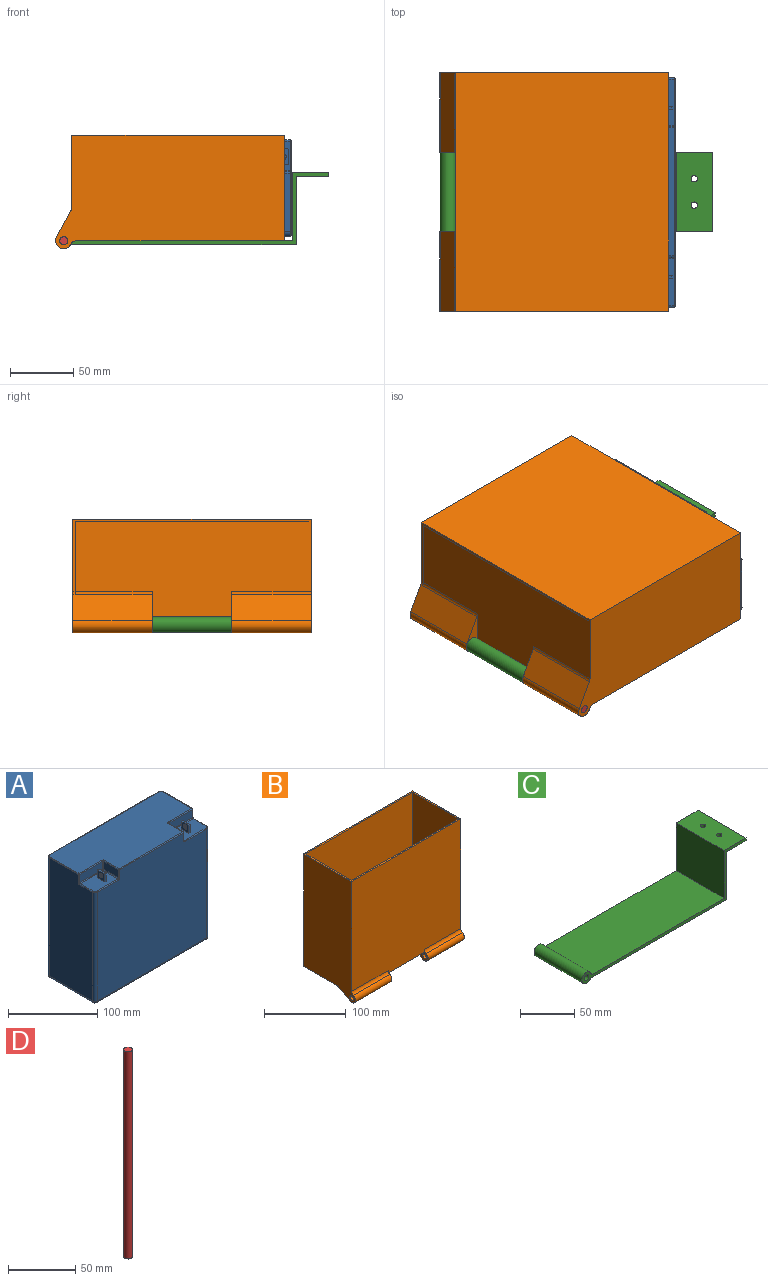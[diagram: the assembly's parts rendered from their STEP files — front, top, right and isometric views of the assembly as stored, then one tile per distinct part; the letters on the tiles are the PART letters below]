
ASSEMBLY  parts=4 mates=3
PART A: 78 faces, bbox 181.6x76.6x167 mm
  f0: plane 179x74mm, normal (0,0,1), area 11284.4mm2, adj f49,f50,f54,f59,f64,f68,f69,f71
  f1: plane 173.8x162.4mm, normal (0,-1,0), area 27282.9mm2, adj f28,f30,f31,f40,f44,f48,f52,f56
  f2: plane 173.8x162.4mm, normal (0,1,0), area 28225.1mm2, adj f33,f37,f39,f72
  f3: plane 162.4x68.8mm, normal (-1,0,0), area 10880.1mm2, adj f30,f36,f39,f47,f51,f55,f64
  f4: plane 162.4x68.8mm, normal (1,0,0), area 10880.2mm2, adj f28,f32,f33,f65,f70,f73,f77
  f5: plane 173.8x68.8mm, normal (0,0,-1), area 11957.4mm2, adj f31,f32,f36,f37
  f6: plane 37.4x23.2mm, normal (0,0,1), area 842.2mm2, adj f12,f13,f14,f15,f56,f57,f61,f65
  f7: plane 37.4x11mm, normal (0,-1,0), area 411.4mm2, adj f66,f67,f73,f74
  f8: plane 23.2x11mm, normal (1,0,0), area 255.2mm2, adj f57,f58,f67,f68
  f9: plane 36.4x23.2mm, normal (0,0,1), area 818.9mm2, adj f20,f21,f22,f23,f40,f41,f43,f46
  f10: plane 36.4x11.01mm, normal (0,-1,0), area 400.6mm2, adj f45,f46,f54,f55
  f11: plane 23.2x11.01mm, normal (-1,0,0), area 255.3mm2, adj f41,f45,f48,f49
  f12: plane 12x11mm, normal (-1,0,0), area 107.8mm2, adj f6,f13,f15,f16,f17,f18,f19
  f13: plane 10x2mm, normal (0,-1,0), area 20mm2, adj f6,f12,f14,f17
  f14: plane 12x11mm, normal (1,0,0), area 107.8mm2, adj f6,f13,f15,f16,f17,f18,f19
  f15: plane 10x2mm, normal (0,1,0), area 20mm2, adj f6,f12,f14,f18
  f16: plane 10x2mm, normal (0,0,1), area 20mm2, adj f12,f14,f17,f18
  f17: cylinder r=1mm len=2mm, axis (-1,0,0), area 3.1mm2, adj f12,f13,f14,f16
  f18: cylinder r=1mm len=2mm, axis (1,0,0), area 3.1mm2, adj f12,f14,f15,f16
  f19: cylinder r=2.75mm len=5.5mm, axis (1,0,0), area 34.6mm2, adj f12,f14
  f20: plane 11.99x11mm, normal (-1,0,0), area 107.7mm2, adj f9,f21,f23,f24,f25,f26,f27
  f21: plane 10x2mm, normal (0,-1,0), area 20mm2, adj f9,f20,f22,f25
  f22: plane 11.99x11mm, normal (1,0,0), area 107.7mm2, adj f9,f21,f23,f24,f25,f26,f27
  f23: plane 10x2mm, normal (0,1,0), area 20mm2, adj f9,f20,f22,f26
  f24: plane 9.99x2mm, normal (0,0,1), area 20mm2, adj f20,f22,f25,f26
  f25: cylinder r=1mm len=2mm, axis (-1,0,0), area 3.1mm2, adj f20,f21,f22,f24
  f26: cylinder r=1mm len=2mm, axis (1,0,0), area 3.1mm2, adj f20,f22,f23,f24
  f27: cylinder r=2.75mm len=5.5mm, axis (-1,0,0), area 34.6mm2, adj f20,f22
  f28: cylinder r=3.6mm len=149.4mm, axis (0,0,1), area 844.8mm2, adj f1,f4,f29,f61
  f29: sphere r=3.6mm, area 20.4mm2, adj f28,f31,f32
  f30: cylinder r=3.6mm len=149.4mm, axis (0,0,-1), area 844.8mm2, adj f1,f3,f34,f43
  f31: cylinder r=3.6mm len=173.8mm, axis (1,0,0), area 982.8mm2, adj f1,f5,f29,f34
  f32: cylinder r=3.6mm len=68.8mm, axis (0,1,0), area 389.1mm2, adj f4,f5,f29,f35
  f33: cylinder r=3.6mm len=162.4mm, axis (0,0,-1), area 918.4mm2, adj f2,f4,f35,f75
  f34: sphere r=3.6mm, area 20.4mm2, adj f30,f31,f36
  f35: sphere r=3.6mm, area 20.4mm2, adj f32,f33,f37
  f36: cylinder r=3.6mm len=68.8mm, axis (0,-1,0), area 389.1mm2, adj f3,f5,f34,f38
  f37: cylinder r=3.6mm len=173.8mm, axis (-1,0,0), area 982.8mm2, adj f2,f5,f35,f38
  f38: sphere r=3.6mm, area 20.4mm2, adj f36,f37,f39
  f39: cylinder r=3.6mm len=162.4mm, axis (0,0,1), area 918.4mm2, adj f2,f3,f38,f69
  f40: cylinder r=1mm len=33.8mm, axis (1,0,0), area 53.1mm2, adj f1,f9,f43,f44
  f41: cylinder r=1mm len=23.2mm, axis (0,-1,0), area 36.4mm2, adj f9,f11,f42,f44
  f42: sphere r=1mm, area 1.6mm2, adj f41,f45,f46
  f43: torus R=2.6mm, axis (0,0,1), area 8mm2, adj f9,f30,f40,f47
  f44: torus R=2mm, axis (0,1,0), area 3.4mm2, adj f1,f40,f41,f48
  f45: cylinder r=1mm len=11.01mm, axis (0,0,-1), area 17.3mm2, adj f10,f11,f42,f50
  f46: cylinder r=1mm len=36.4mm, axis (-1,0,0), area 57.2mm2, adj f9,f10,f42,f51
  f47: cylinder r=1mm len=20.6mm, axis (0,-1,0), area 32.4mm2, adj f3,f9,f43,f51
  f48: cylinder r=1mm len=11.01mm, axis (0,0,1), area 17.3mm2, adj f1,f11,f44,f53
  f49: cylinder r=1mm len=23.2mm, axis (0,-1,0), area 36.4mm2, adj f0,f11,f50,f53
  f50: torus R=2mm, axis (0,0,1), area 3.4mm2, adj f0,f45,f49,f54
  f51: torus R=2mm, axis (1,0,0), area 3.4mm2, adj f3,f46,f47,f55
  f52: torus R=2mm, axis (0,1,0), area 3.4mm2, adj f1,f56,f57,f58
  f53: sphere r=1mm, area 1.6mm2, adj f48,f49,f59
  f54: cylinder r=1mm len=36.4mm, axis (1,0,0), area 57.2mm2, adj f0,f10,f50,f60
  f55: cylinder r=1mm len=11.01mm, axis (0,0,-1), area 17.3mm2, adj f3,f10,f51,f60
  f56: cylinder r=1mm len=34.8mm, axis (1,0,0), area 54.7mm2, adj f1,f6,f52,f61
  f57: cylinder r=1mm len=23.2mm, axis (0,1,0), area 36.4mm2, adj f6,f8,f52,f62
  f58: cylinder r=1mm len=11mm, axis (0,0,1), area 17.3mm2, adj f1,f8,f52,f63
  f59: cylinder r=1mm len=101.2mm, axis (-1,0,0), area 159mm2, adj f0,f1,f53,f63
  f60: sphere r=1mm, area 1.6mm2, adj f54,f55,f64
  f61: torus R=2.6mm, axis (0,0,-1), area 8mm2, adj f6,f28,f56,f65
  f62: sphere r=1mm, area 1.6mm2, adj f57,f66,f67
  f63: sphere r=1mm, area 1.6mm2, adj f58,f59,f68
  f64: cylinder r=1mm len=46.2mm, axis (0,1,0), area 72.6mm2, adj f0,f3,f60,f69
  f65: cylinder r=1mm len=20.6mm, axis (0,-1,0), area 32.4mm2, adj f4,f6,f61,f70
  f66: cylinder r=1mm len=37.4mm, axis (1,0,0), area 58.7mm2, adj f6,f7,f62,f70
  f67: cylinder r=1mm len=11mm, axis (0,0,1), area 17.3mm2, adj f7,f8,f62,f71
  f68: cylinder r=1mm len=23.2mm, axis (0,-1,0), area 36.4mm2, adj f0,f8,f63,f71
  f69: torus R=2.6mm, axis (0,0,1), area 8mm2, adj f0,f39,f64,f72
  f70: torus R=2mm, axis (1,0,0), area 3.4mm2, adj f4,f65,f66,f73
  f71: torus R=2mm, axis (0,0,1), area 3.4mm2, adj f0,f67,f68,f74
  f72: cylinder r=1mm len=173.8mm, axis (1,0,0), area 273mm2, adj f0,f2,f69,f75
  f73: cylinder r=1mm len=11mm, axis (0,0,-1), area 17.3mm2, adj f4,f7,f70,f76
  f74: cylinder r=1mm len=37.4mm, axis (1,0,0), area 58.7mm2, adj f0,f7,f71,f76
  f75: torus R=2.6mm, axis (0,0,1), area 8mm2, adj f0,f33,f72,f77
  f76: sphere r=1mm, area 1.6mm2, adj f73,f74,f77
  f77: cylinder r=1mm len=46.2mm, axis (0,-1,0), area 72.6mm2, adj f0,f4,f75,f76
PART B: 27 faces, bbox 188.2x89.5x180.7 mm
  f0: plane 188.18x83.18mm, normal (0,0,-1), area 12374.2mm2, adj f1,f2,f3,f4,f5,f6,f7,f10
  f1: plane 168x79.22mm, normal (1,0,0), area 12805.3mm2, adj f0,f2,f8,f9,f11,f12
  f2: plane 184.21x168mm, normal (0,-1,0), area 30947.9mm2, adj f0,f1,f3,f9
  f3: plane 168.63x79.21mm, normal (-1,0,0), area 13308.2mm2, adj f0,f2,f8,f9,f13,f15,f18
  f4: plane 180.7x89.53mm, normal (-1,0,0), area 14174.8mm2, adj f0,f5,f7,f9,f20,f21,f22,f24
  f5: plane 188.18x168mm, normal (0,-1,0), area 31125.5mm2, adj f0,f4,f6,f9,f17,f19,f23,f25
  f6: plane 180.7x89.53mm, normal (1,0,0), area 14174.8mm2, adj f0,f5,f7,f9,f14,f15,f16,f18
  f7: plane 188.18x168mm, normal (0,1,0), area 31613.4mm2, adj f0,f4,f6,f9
  f8: plane 184.22x168mm, normal (0,1,0), area 29778.4mm2, adj f1,f3,f9,f10,f12,f13
  f9: plane 188.18x83.18mm, normal (0,0,1), area 1059.1mm2, adj f1,f2,f3,f4,f5,f6,f7,f8
  f10: plane 79.17x6.98mm, normal (1,0,0), area 502.8mm2, adj f0,f8,f11,f12,f13,f15,f26
  f11: plane 184.17x6.35mm, normal (0,1,0), area 1169.5mm2, adj f0,f1,f10,f12
  f12: plane 184.17x79.17mm, normal (0,0,1), area 14580mm2, adj f1,f8,f10,f11
  f13: plane 22.72x0.04mm, normal (0,0,1), area 0.9mm2, adj f3,f8,f10,f15
  f14: cylinder r=6.35mm len=62.73mm, axis (1,0,0), area 1268.1mm2, adj f6,f15,f17,f19
  f15: plane 62.73x21.67mm, normal (0,0.48,-0.88), area 1469.3mm2, adj f3,f6,f10,f13,f14,f17,f18,f26
  f16: cylinder r=3.17mm len=62.73mm, axis (1,0,0), area 1251.3mm2, adj f6,f17
  f17: plane 32.38x16.59mm, normal (-1,0,0), area 201.4mm2, adj f0,f5,f14,f15,f16,f19,f26
  f18: cylinder r=5.08mm len=2.45mm, axis (-1,0,0), area 5mm2, adj f0,f3,f6,f15
  f19: cylinder r=5.08mm len=62.73mm, axis (1,0,0), area 353.8mm2, adj f5,f6,f14,f17
  f20: plane 62.73x20.53mm, normal (0,0.48,-0.88), area 1469.3mm2, adj f4,f21,f23,f24
  f21: cylinder r=6.35mm len=62.73mm, axis (-1,0,0), area 1268.1mm2, adj f4,f20,f23,f25
  f22: cylinder r=3.17mm len=62.73mm, axis (-1,0,0), area 1251.3mm2, adj f4,f23
  f23: plane 32.38x16.59mm, normal (1,0,0), area 201.4mm2, adj f0,f5,f20,f21,f22,f24,f25
  f24: cylinder r=5.08mm len=62.73mm, axis (-1,0,0), area 160.2mm2, adj f0,f4,f20,f23
  f25: cylinder r=5.08mm len=62.73mm, axis (-1,0,0), area 353.8mm2, adj f4,f5,f21,f23
  f26: cylinder r=5.08mm len=60.73mm, axis (-1,0,0), area 155.1mm2, adj f0,f10,f15,f17
PART C: 14 faces, bbox 214.9x62.7x60.1 mm
  f0: plane 175.85x62.73mm, normal (0,0,-1), area 11030.5mm2, adj f1,f9,f10,f11
  f1: plane 62.73x53.98mm, normal (1,0,0), area 3385.6mm2, adj f0,f2,f9,f10
  f2: plane 62.73x25.4mm, normal (0,0,-1), area 1552.7mm2, adj f1,f3,f9,f10,f12,f13
  f3: plane 62.73x3.18mm, normal (1,0,0), area 199.2mm2, adj f2,f4,f9,f10
  f4: plane 62.73x28.58mm, normal (0,0,1), area 1751.8mm2, adj f3,f5,f9,f10,f12,f13
  f5: plane 62.73x53.98mm, normal (-1,0,0), area 3385.6mm2, adj f4,f6,f9,f10
  f6: plane 174.12x62.73mm, normal (0,0,1), area 10921.5mm2, adj f5,f7,f9,f10
  f7: cylinder r=6.1mm len=62.73mm, axis (0,1,0), area 2084.7mm2, adj f6,f9,f10,f11
  f8: cylinder r=3.05mm len=62.73mm, axis (0,1,0), area 1201.3mm2, adj f9,f10
  f9: plane 214.88x60.07mm, normal (0,-1,0), area 904mm2, adj f0,f1,f2,f3,f4,f5,f6,f7
  f10: plane 214.88x60.07mm, normal (0,1,0), area 904mm2, adj f0,f1,f2,f3,f4,f5,f6,f7
  f11: cylinder r=5.08mm len=62.73mm, axis (0,1,0), area 235.7mm2, adj f0,f7,f9,f10
  f12: cylinder r=2.54mm len=5.08mm, axis (0,0,1), area 50.7mm2, adj f2,f4
  f13: cylinder r=2.54mm len=5.08mm, axis (0,0,1), area 50.7mm2, adj f2,f4
PART D: 3 faces, bbox 6.4x6.4x188.2 mm
  f0: cylinder r=3.17mm len=188.18mm, axis (0,0,-1), area 3753.9mm2, adj f1,f2
  f1: plane 6.35x6.35mm, normal (0,0,1), area 31.7mm2, adj f0
  f2: plane 6.35x6.35mm, normal (0,0,-1), area 31.7mm2, adj f0
PLACE A rot(axis=(-0.58,0.58,-0.58),120deg) t=(-12.7,1.39,33.69)mm
PLACE B rot(axis=(0.58,0.58,0.58),120deg) t=(-19.05,-4.76,33.87)mm
PLACE C t=(27.9,26.6,-22.15)mm fixed
PLACE D rot(axis=(1,0,0),90deg) t=(48.6,89.33,-30.8)mm
MATE fastened B.f12 <-> A.f5  axis (1,0,0) through (-12.7,-96.85,33.87)mm
MATE fastened D.f0 <-> B.f21  axis (0,1,0) through (-25.4,-98.85,-7.72)mm
MATE revolute B.f21 <-> C.f7  axis (0,1,0) through (-25.4,-36.12,-7.72)mm
